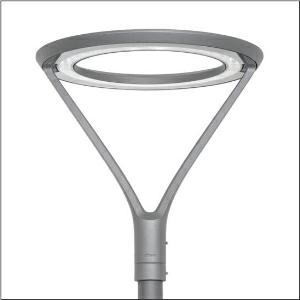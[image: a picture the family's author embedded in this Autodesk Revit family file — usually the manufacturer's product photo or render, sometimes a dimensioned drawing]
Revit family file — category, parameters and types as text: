
# Revit family: dl_r__20___pl1_2s_5xa51283ns008_3424
name_source: partatom
category: Lighting Fixtures
units: mm (PartAtom-declared; Revit-internal decimal feet)

## family parameters
Cut with Voids When Loaded = No
Host = Face
Light Source = No
Part Type = Normal
Room Calculation Point = No
Round Connector Dimension = Use Diameter
Shared = No

## types (1)
- --- (1 x LED, 3060 lm, 23.2 W, 4000K)
    Apparent Load = 23 VA
    CIE Flux Codes = 33 78 99 100 100
    Color Rendering = 70
    Color Temperature = 4000K
    Default Elevation = 1800 mm
    Description = DL® 20, mast luminaire, primary light control with reflector, highly specular, primary optical cover: cover, of toughened safety glass of clear glass with excellent transmission level, light distribution: PL1.2s, light emission: direct distribution, primary light characteristic: symmetric, installation type: post-top, LED, High Power LED, rated luminous flux: 3.030lm, luminous efficacy: 111lm/W, light colour: 740, colour temperature: 4000K, control gear: ECG Plus, control: overheat protection, power reduction, digital communication interface, constant luminous flux control, time-dependent luminous flux control, flexible luminous flux parameterisation, electronic power reduction, mains connection: 230..240V, 50/60Hz, connection cable pre-assembled, cable length: 5m, start of lifetime: 27W, end of service life: 28W, reduction: 14W, luminaire housing, upper part, of cast aluminium, powder-coated, Siteco® metallic grey (DB 702S), diameter: 690mm, height: 690mm, spigot size: 76mm (post-top), luminaire housing, of cast aluminium, powder-coated, Siteco® metallic grey (DB 702S), equipment: standard, protection rating (complete): IP66, insulation class (complete): insulation class II (safety insulation), certification: CE, ENEC, VDE, impact resistance: IK08, permissible operating ambient temperature: -25..+35°C, standard-compliant lighting for roads and squares, packaging unit: 1 piece

Light Distribution: PL1.2s
    Height = 690 mm
    Lamp = 1 x LED
    Lamp Light Flux = 3060 lm
    Lamp Power = 23.2 W
    Lamp count = 1
    Length = 690 mm
    Luminous efficacy = 132 lm/W
    Manufacturer = Siteco
    ModVariant = No
    Model = 5XA51283NS008
    Number of Poles = 1
    OnlyDefault = Yes
    Power Factor = 1
    Product Name = DL® 20 | PL1.2s
    Product group = mast luminaire | pylon top
    ProductGroupID = 6100
    Protection Class = Protection class II
    Protection Degree = IP 66
    RLX_Detail_Level = 1
    RLX_Emergency_Light_Flux = 0 lm
    RLX_Emergency_Type = 0
    RLX_Emergency_Type_DB = No
    RlxData = <blob elided: 205081 chars, md5=70c3bf35>
    Socket = socket
    Standby Power = 0 W
    System Light Flux = 3060 lm
    System Power = 23 W
    Type Comments = factory setting: luminous flux: 100 % | dim-lin: 254 | 310 mA
    Type Image = l_1006001.jpg
    URL = http://relux.com
    VarID = @adj_027795
    Voltage = 0 V
    Weight = 0.00 kg
    Width = 0 mm  [stored 0 ft]

note: [stored X ft] marks values corroborated as IEEE doubles in the binary element streams (Revit-internal decimal feet)

## geometry (parser evidence)
native form markers: Blend x4, Sweep x9
no freeform markers — native parametric forms only
